# Revit family: Gleiter radial-axial GL-37
name_source: partatom
category: HLS-Bauteile
revit_build: Autodesk Revit 2017 (Build: 20190507_1515(x64)
units: mm (PartAtom-declared; Revit-internal decimal feet)

## family parameters
Arbeitsebenenbasiert = Ja
Beim Laden mit Abzugskörper schneiden = Nein
Bemaßung runder Anschluss = Durchmesser verwenden
Gemeinsam genutzt = Ja
Immer vertikal = Nein
Raumberechnungspunkt = Nein
Teiletyp = Normal

## types (5) — shared parameters
B1 = 36 mm  [stored 0.11811 ft]
Breite = 72 mm  [stored 0.23622 ft]
D0 = 14 mm  [stored 0.0459318 ft]
Fabrikat = MEFA
Firma = MEFA Befestigungs- und Montagesysteme GmbH
Gleitreibungsfaktor = 0.15 - 0.25
H = 18 mm  [stored 0.0590551 ft]
H1 = 22 mm  [stored 0.0721785 ft]
Haftreibungsfaktor = 0,2 - 0,3
Kurztext1 = Gleitelement radial-axial GL 37
L = 72 mm  [stored 0.23622 ft]
Länge = 72 mm  [stored 0.23622 ft]
Material Gleitstreifen = Kunststoff
Materialname Gleitstreifen = Polyamid 6
Mengeneinheit = St
Vorgabe-Ansicht = 1219 mm
max. Temperaturbeständigkeit = 100 °C
vpe = 1 St

## per-type parameters (varying)
| type | Artikelnummer | EAN | GL-37 | Gewicht | Gewicht pro Bauteil | Kurztext2 |
| Gleiter ra-ax GL 37, M 8 | 077046801 | 4250928417596 | Gleiter GL-37 : Gleiter GL-37, AG M 8 | 0.36 kg | 0.36 kg | Anschluss 1 x M8 |
| Gleiter ra-ax GL 37, M10 | 077046001 | 4250928417558 | Gleiter GL-37 : Gleiter GL-37, AG M10 | 0.37 kg | 0.37 kg | Anschluss 1 x M10 |
| Gleiter ra-ax GL 37, M12 | 077046201 | 4250928417565 | Gleiter GL-37 : Gleiter GL-37, AG M12 | 0.38 kg | 0.38 kg | Anschluss 1 x M12 |
| Gleiter ra-ax GL 37, M16 | 077046601 | 4250928417589 | Gleiter GL-37 : Gleiter GL-37, AG M16 | 0.39 kg | 0.39 kg | Anschluss 1 x M16 |
| Gleiter ra-ax GL 37, 1/2" | 077046401 | 4250928417572 | Gleiter GL-37 : Gleiter GL-37, AG Muffe halb Zoll | 0.38 kg | 0.38 kg | Anschluss 1 x 1/2'' |

note: [stored X ft] marks values corroborated as IEEE doubles in the binary element streams (Revit-internal decimal feet)

## geometry (parser evidence)
native form markers: Sweep x3
no freeform markers — native parametric forms only
